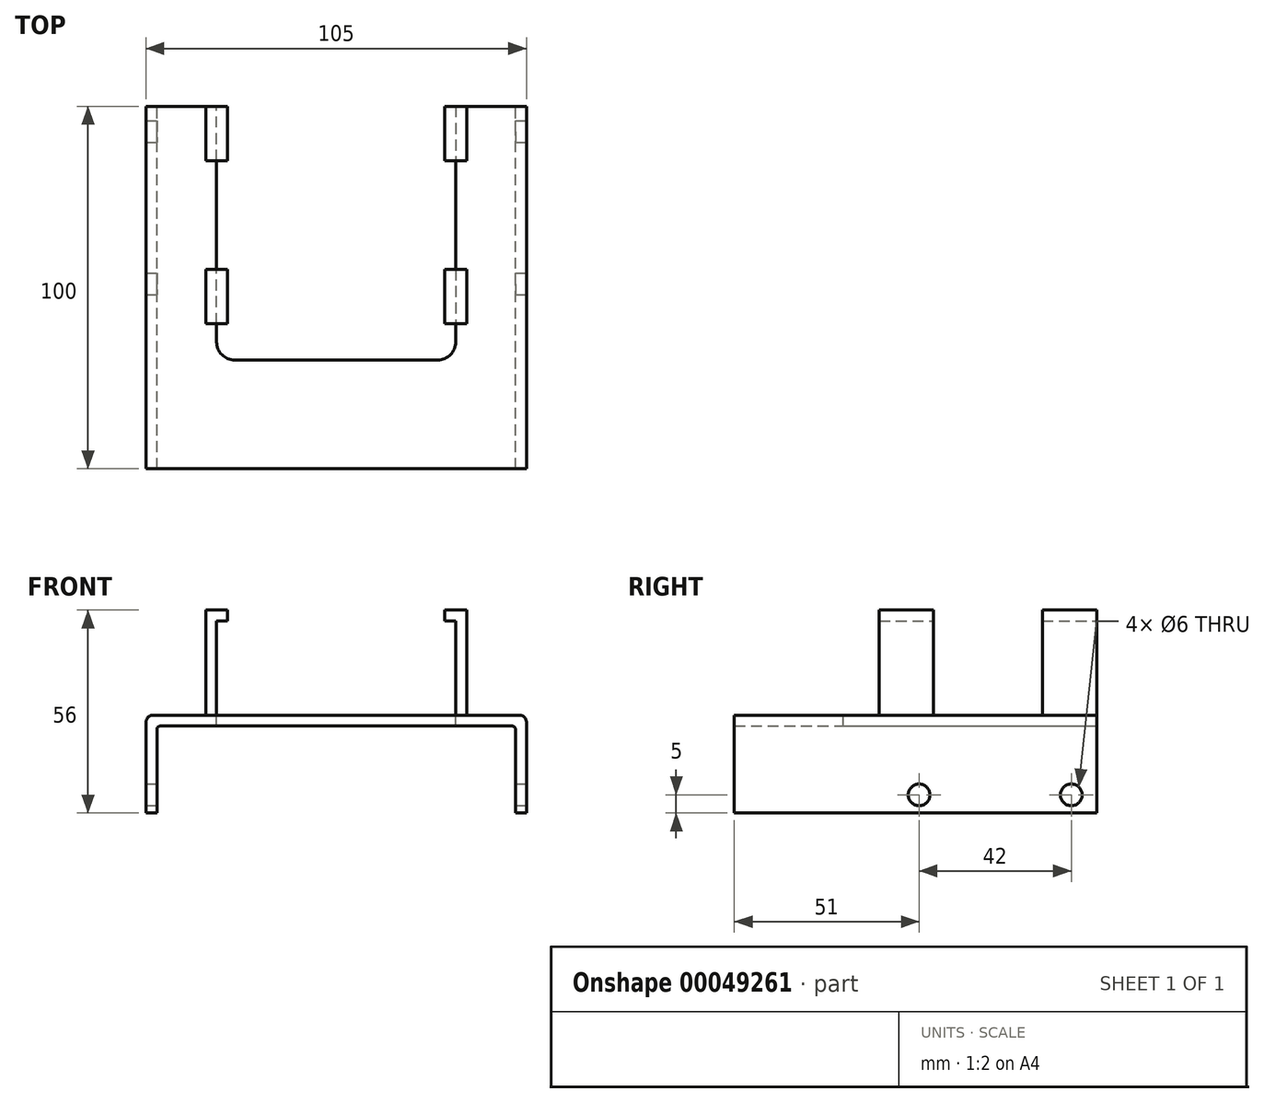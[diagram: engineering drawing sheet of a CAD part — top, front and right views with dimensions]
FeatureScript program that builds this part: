
annotation { "Feature Type Name" : "Feature", "Feature Type Description" : "" }
export const myFeature = defineFeature(function(context is Context, id is Id, definition is map)
    precondition{}
    {
        {
            var Q0;
            Q0=qCreatedBy(makeId("Front.planeOp"),FACE);
            var sketch = newSketch(context, id + "F0", { "sketchPlane" : qUnion([Q0])});
            skLineSegment(sketch, "E0", {"start": v(0, 27) * mm, "end": v(105, 27) * mm});
            skLineSegment(sketch, "E1", {"start": v(102, 0) * mm, "end": v(102, 24) * mm});
            skLineSegment(sketch, "E2", {"start": v(102, 24) * mm, "end": v(3, 24) * mm});
            skLineSegment(sketch, "E3", {"start": v(3, 24) * mm, "end": v(3, 0) * mm});
            skLineSegment(sketch, "E4", {"start": v(102, 0) * mm, "end": v(105, 0) * mm});
            skLineSegment(sketch, "E5", {"start": v(105, 27) * mm, "end": v(105, 0) * mm});
            skLineSegment(sketch, "E6", {"start": v(3, 0) * mm, "end": v(0, 0) * mm});
            skLineSegment(sketch, "E7", {"start": v(0, 27) * mm, "end": v(0, 0) * mm});
            skSolve(sketch);
        }
        {
            var Q0;
            Q0=qSketchRegion(id+"F0",true);
            extrude(context, id + "F1", {"entities" : qUnion([Q0]), "depth" : 100 * mm});
        }
        {
            var Q0;
            Q0=makeQuery(id+"F1.opExtrude","SWEPT_FACE",FACE,{"disambiguationData":[OSD([sQuery(id+"F0.wireOp",EDGE,"E5")])]});
            var sketch = newSketch(context, id + "F2", { "sketchPlane" : qUnion([Q0])});
            skCircle(sketch, "E8", {"center": v(-7, 5) * mm, "radius": 3 * mm});
            skCircle(sketch, "E9", {"center": v(-49, 5) * mm, "radius": 3 * mm});
            skSolve(sketch);
        }
        {
            var Q0;
            Q0=qSketchRegion(id+"F2",true);
            extrude(context, id + "F3", {"entities" : qUnion([Q0]), "operationType" : NewBodyOperationType.REMOVE, "endBound" : BoundingType.THROUGH_ALL, "oppositeDirection" : true, "depth" : 25 * mm});
        }
        {
            var Q0;
            Q0=makeQuery(id+"F1.opExtrude","SWEPT_FACE",FACE,{"disambiguationData":[OSD([sQuery(id+"F0.wireOp",EDGE,"E0")])]});
            var sketch = newSketch(context, id + "F4", { "sketchPlane" : qUnion([Q0])});
            skLineSegment(sketch, "E10.bottom", {"start": v(19.5, 0) * mm, "end": v(85.5, 0) * mm});
            skLineSegment(sketch, "E10.top", {"start": v(19.5, -70) * mm, "end": v(85.5, -70) * mm});
            skLineSegment(sketch, "E10.left", {"start": v(19.5, 0) * mm, "end": v(19.5, -70) * mm});
            skLineSegment(sketch, "E10.right", {"start": v(85.5, 0) * mm, "end": v(85.5, -70) * mm});
            skSolve(sketch);
        }
        {
            var Q0;
            Q0=qSketchRegion(id+"F4",true);
            extrude(context, id + "F5", {"entities" : qUnion([Q0]), "operationType" : NewBodyOperationType.REMOVE, "oppositeDirection" : true, "depth" : 25 * mm});
        }
        {
            var Q0;
            Q0=makeQuery(id+"F1.opExtrude","SWEPT_FACE",FACE,{"disambiguationData":[OSD([sQuery(id+"F0.wireOp",EDGE,"E0")])]});
            var sketch = newSketch(context, id + "F6", { "sketchPlane" : qUnion([Q0])});
            skLineSegment(sketch, "E11.bottom", {"start": v(19.5, 0) * mm, "end": v(16.5, 0) * mm});
            skLineSegment(sketch, "E11.top", {"start": v(19.5, -15) * mm, "end": v(16.5, -15) * mm});
            skLineSegment(sketch, "E11.left", {"start": v(19.5, 0) * mm, "end": v(19.5, -15) * mm});
            skLineSegment(sketch, "E11.right", {"start": v(16.5, 0) * mm, "end": v(16.5, -15) * mm});
            skLineSegment(sketch, "E12.bottom", {"start": v(19.5, -45) * mm, "end": v(16.5, -45) * mm});
            skLineSegment(sketch, "E12.top", {"start": v(19.5, -60) * mm, "end": v(16.5, -60) * mm});
            skLineSegment(sketch, "E12.left", {"start": v(19.5, -45) * mm, "end": v(19.5, -60) * mm});
            skLineSegment(sketch, "E12.right", {"start": v(16.5, -45) * mm, "end": v(16.5, -60) * mm});
            skLineSegment(sketch, "E13.bottom", {"start": v(85.5, 0) * mm, "end": v(88.5, 0) * mm});
            skLineSegment(sketch, "E13.top", {"start": v(85.5, -15) * mm, "end": v(88.5, -15) * mm});
            skLineSegment(sketch, "E13.left", {"start": v(85.5, 0) * mm, "end": v(85.5, -15) * mm});
            skLineSegment(sketch, "E13.right", {"start": v(88.5, 0) * mm, "end": v(88.5, -15) * mm});
            skPoint(sketch, "E14.firstSnap0", {"position": v(85.5, -35) * mm});
            skLineSegment(sketch, "E14.bottom", {"start": v(85.5, -45) * mm, "end": v(88.5, -45) * mm});
            skLineSegment(sketch, "E14.top", {"start": v(85.5, -60) * mm, "end": v(88.5, -60) * mm});
            skLineSegment(sketch, "E14.left", {"start": v(85.5, -45) * mm, "end": v(85.5, -60) * mm});
            skLineSegment(sketch, "E14.right", {"start": v(88.5, -45) * mm, "end": v(88.5, -60) * mm});
            skSolve(sketch);
        }
        {
            var Q0;
            Q0=qSketchRegion(id+"F6",true);
            extrude(context, id + "F7", {"entities" : qUnion([Q0]), "operationType" : NewBodyOperationType.ADD, "depth" : 29 * mm});
        }
        {
            var Q0;
            Q0=makeQuery(id+"F7.boolean.opBoolean","MERGE",FACE,{"derivedFrom":[makeQuery(id+"F5.boolean.opBoolean","COPY",FACE,{"derivedFrom":makeQuery(id+"F5.opExtrude","SWEPT_FACE",FACE,{"disambiguationData":[OSD([sQuery(id+"F4.wireOp",EDGE,"E10.left")])]})}),makeQuery(id+"F7.opExtrude","SWEPT_FACE",FACE,{"disambiguationData":[OSD([sQuery(id+"F6.wireOp",EDGE,"E11.left")])]}),makeQuery(id+"F7.opExtrude","SWEPT_FACE",FACE,{"disambiguationData":[OSD([sQuery(id+"F6.wireOp",EDGE,"E12.left")])]})]});
            var sketch = newSketch(context, id + "F8", { "sketchPlane" : qUnion([Q0])});
            skLineSegment(sketch, "E15.bottom", {"start": v(-60, 56) * mm, "end": v(-45, 56) * mm});
            skLineSegment(sketch, "E15.top", {"start": v(-60, 53) * mm, "end": v(-45, 53) * mm});
            skLineSegment(sketch, "E15.left", {"start": v(-60, 56) * mm, "end": v(-60, 53) * mm});
            skLineSegment(sketch, "E15.right", {"start": v(-45, 56) * mm, "end": v(-45, 53) * mm});
            skLineSegment(sketch, "E16.bottom", {"start": v(-15, 56) * mm, "end": v(0, 56) * mm});
            skLineSegment(sketch, "E16.top", {"start": v(-15, 53) * mm, "end": v(0, 53) * mm});
            skLineSegment(sketch, "E16.left", {"start": v(-15, 56) * mm, "end": v(-15, 53) * mm});
            skLineSegment(sketch, "E16.right", {"start": v(0, 56) * mm, "end": v(0, 53) * mm});
            skSolve(sketch);
        }
        {
            var Q0;
            Q0=qSketchRegion(id+"F8",true);
            extrude(context, id + "F9", {"entities" : qUnion([Q0]), "operationType" : NewBodyOperationType.ADD, "depth" : 3 * mm});
        }
        {
            var Q0;
            Q0=makeQuery(id+"F7.boolean.opBoolean","MERGE",FACE,{"derivedFrom":[makeQuery(id+"F5.boolean.opBoolean","COPY",FACE,{"derivedFrom":makeQuery(id+"F5.opExtrude","SWEPT_FACE",FACE,{"disambiguationData":[OSD([sQuery(id+"F4.wireOp",EDGE,"E10.right")])]})}),makeQuery(id+"F7.opExtrude","SWEPT_FACE",FACE,{"disambiguationData":[OSD([sQuery(id+"F6.wireOp",EDGE,"E13.left")])]}),makeQuery(id+"F7.opExtrude","SWEPT_FACE",FACE,{"disambiguationData":[OSD([sQuery(id+"F6.wireOp",EDGE,"E14.left")])]})]});
            var sketch = newSketch(context, id + "F10", { "sketchPlane" : qUnion([Q0])});
            skLineSegment(sketch, "E17.bottom", {"start": v(0, 56) * mm, "end": v(15, 56) * mm});
            skLineSegment(sketch, "E17.top", {"start": v(0, 53) * mm, "end": v(15, 53) * mm});
            skLineSegment(sketch, "E17.left", {"start": v(0, 56) * mm, "end": v(0, 53) * mm});
            skLineSegment(sketch, "E17.right", {"start": v(15, 56) * mm, "end": v(15, 53) * mm});
            skLineSegment(sketch, "E18.bottom", {"start": v(45, 56) * mm, "end": v(60, 56) * mm});
            skLineSegment(sketch, "E18.top", {"start": v(45, 53) * mm, "end": v(60, 53) * mm});
            skLineSegment(sketch, "E18.left", {"start": v(45, 56) * mm, "end": v(45, 53) * mm});
            skLineSegment(sketch, "E18.right", {"start": v(60, 56) * mm, "end": v(60, 53) * mm});
            skSolve(sketch);
        }
        {
            var Q0;
            Q0=qSketchRegion(id+"F10",true);
            extrude(context, id + "F11", {"entities" : qUnion([Q0]), "operationType" : NewBodyOperationType.ADD, "depth" : 3 * mm});
        }
        {
            var Q0;
            Q0=makeQuery(id+"F1.opExtrude","SWEPT_EDGE",EDGE,{"disambiguationData":[OSD([sQuery(id+"F0.wireOp",EDGE,"E2"),sQuery(id+"F0.wireOp",EDGE,"E3")])]});
            var Q1;
            Q1=makeQuery(id+"F1.opExtrude","SWEPT_EDGE",EDGE,{"disambiguationData":[OSD([sQuery(id+"F0.wireOp",EDGE,"E1"),sQuery(id+"F0.wireOp",EDGE,"E2")])]});
            var Q2;
            Q2=makeQuery(id+"F7.opExtrude","CAP_EDGE",EDGE,{"disambiguationData":[OSD([sQuery(id+"F6.wireOp",EDGE,"E11.right")])],"isStart":true});
            var Q3;
            Q3=makeQuery(id+"F7.opExtrude","CAP_EDGE",EDGE,{"disambiguationData":[OSD([sQuery(id+"F6.wireOp",EDGE,"E11.top")])],"isStart":true});
            var Q4;
            Q4=makeQuery(id+"F7.opExtrude","CAP_EDGE",EDGE,{"disambiguationData":[OSD([sQuery(id+"F6.wireOp",EDGE,"E12.right")])],"isStart":true});
            var Q5;
            Q5=makeQuery(id+"F7.opExtrude","CAP_EDGE",EDGE,{"disambiguationData":[OSD([sQuery(id+"F6.wireOp",EDGE,"E12.top")])],"isStart":true});
            var Q6;
            Q6=makeQuery(id+"F7.opExtrude","CAP_EDGE",EDGE,{"disambiguationData":[OSD([sQuery(id+"F6.wireOp",EDGE,"E12.bottom")])],"isStart":true});
            var Q7;
            Q7=makeQuery(id+"F7.opExtrude","CAP_EDGE",EDGE,{"disambiguationData":[OSD([sQuery(id+"F6.wireOp",EDGE,"E14.top")])],"isStart":true});
            var Q8;
            Q8=makeQuery(id+"F7.opExtrude","CAP_EDGE",EDGE,{"disambiguationData":[OSD([sQuery(id+"F6.wireOp",EDGE,"E14.right")])],"isStart":true});
            var Q9;
            Q9=makeQuery(id+"F7.opExtrude","CAP_EDGE",EDGE,{"disambiguationData":[OSD([sQuery(id+"F6.wireOp",EDGE,"E13.top")])],"isStart":true});
            var Q10;
            Q10=makeQuery(id+"F7.opExtrude","CAP_EDGE",EDGE,{"disambiguationData":[OSD([sQuery(id+"F6.wireOp",EDGE,"E13.right")])],"isStart":true});
            var Q11;
            Q11=makeQuery(id+"F7.opExtrude","CAP_EDGE",EDGE,{"disambiguationData":[OSD([sQuery(id+"F6.wireOp",EDGE,"E14.bottom")])],"isStart":true});
            fillet(context, id + "F12", {"entities" : qUnion([Q0, Q1, Q2, Q3, Q4, Q5, Q6, Q7, Q8, Q9, Q10, Q11]), "radius" : 1 * mm, "tangentPropagation" : true, "allowEdgeOverflow" : false});
        }
        {
            var Q0;
            Q0=makeQuery(id+"F1.opExtrude","SWEPT_EDGE",EDGE,{"disambiguationData":[OSD([sQuery(id+"F0.wireOp",EDGE,"E0"),sQuery(id+"F0.wireOp",EDGE,"E7")])]});
            var Q1;
            Q1=makeQuery(id+"F1.opExtrude","SWEPT_EDGE",EDGE,{"disambiguationData":[OSD([sQuery(id+"F0.wireOp",EDGE,"E0"),sQuery(id+"F0.wireOp",EDGE,"E5")])]});
            fillet(context, id + "F13", {"entities" : qUnion([Q0, Q1]), "radius" : 2 * mm, "tangentPropagation" : true, "allowEdgeOverflow" : false});
        }
        {
            var Q0;
            Q0=makeQuery(id+"F5.boolean.opBoolean","COPY",EDGE,{"derivedFrom":makeQuery(id+"F5.opExtrude","SWEPT_EDGE",EDGE,{"disambiguationData":[OSD([sQuery(id+"F4.wireOp",EDGE,"E10.top"),sQuery(id+"F4.wireOp",EDGE,"E10.right")])]})});
            var Q1;
            Q1=makeQuery(id+"F5.boolean.opBoolean","COPY",EDGE,{"derivedFrom":makeQuery(id+"F5.opExtrude","SWEPT_EDGE",EDGE,{"disambiguationData":[OSD([sQuery(id+"F4.wireOp",EDGE,"E10.top"),sQuery(id+"F4.wireOp",EDGE,"E10.left")])]})});
            fillet(context, id + "F14", {"entities" : qUnion([Q0, Q1]), "radius" : 5 * mm, "tangentPropagation" : true, "allowEdgeOverflow" : false});
        }
    });
